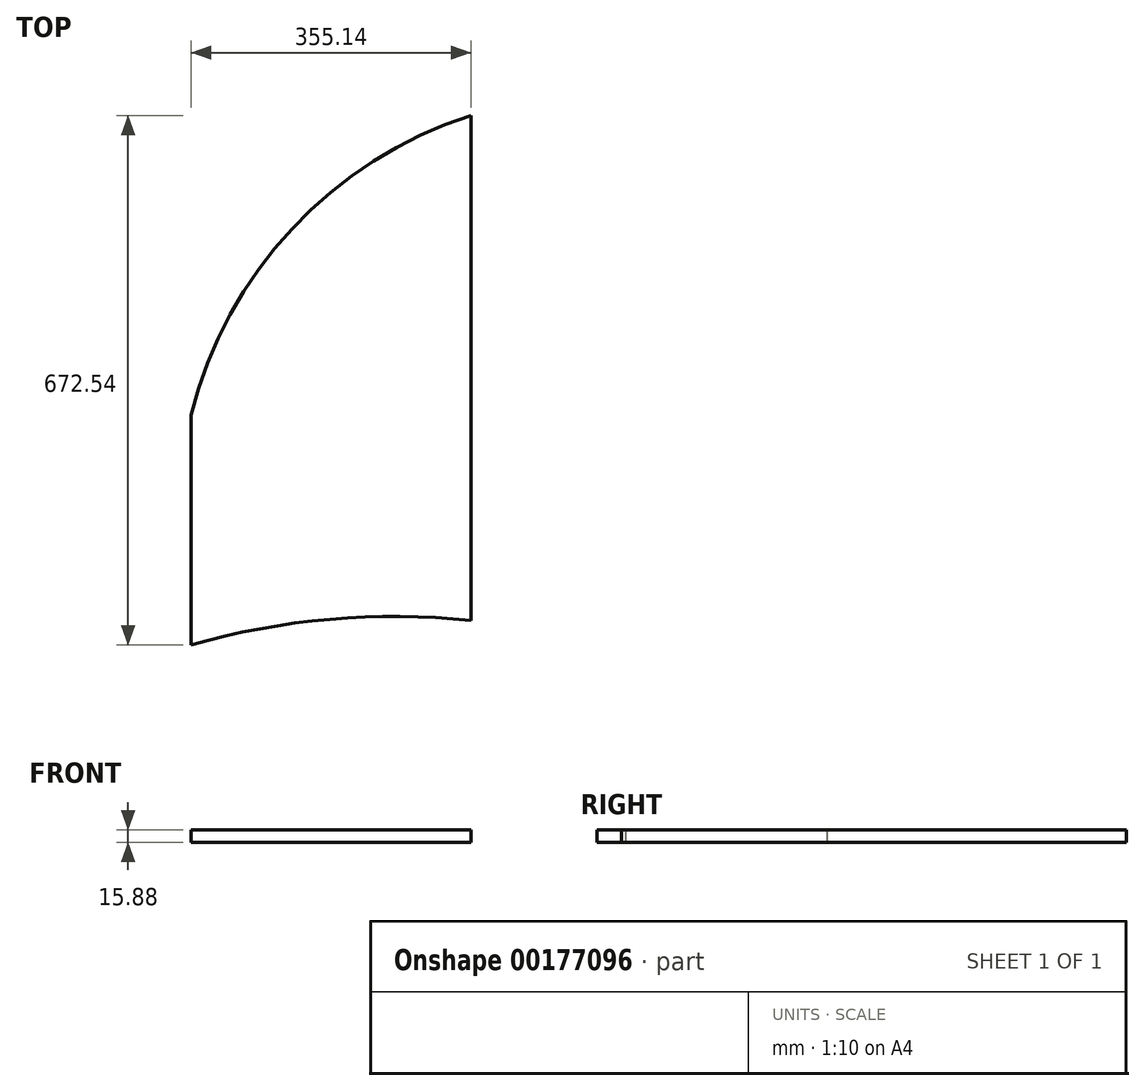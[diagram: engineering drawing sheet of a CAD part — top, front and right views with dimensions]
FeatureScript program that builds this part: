
annotation { "Feature Type Name" : "Feature", "Feature Type Description" : "" }
export const myFeature = defineFeature(function(context is Context, id is Id, definition is map)
    precondition{}
    {
        {
            var Q0;
            Q0=qCreatedBy(makeId("Top.planeOp"),FACE);
            var sketch = newSketch(context, id + "F0", { "sketchPlane" : qUnion([Q0])});
            skLineSegment(sketch, "E0", {"start": v(0, 641.35) * mm, "end": v(0, 0) * mm});
            skArc(sketch, "E1", {"start": v(0, 641.35) * mm, "mid": v(-227.12, 497.38) * mm, "end": v(-355.14, 260.91) * mm});
            skLineSegment(sketch, "E2", {"start": v(-355.14, -31.19) * mm, "end": v(-355.14, 260.91) * mm});
            skArc(sketch, "E3", {"start": v(0, 0) * mm, "mid": v(-179.06, 1.4) * mm, "end": v(-355.14, -31.19) * mm});
            skSolve(sketch);
        }
        {
            var Q0;
            Q0 = qSketchRegion(id + "F0", true);
            extrude(context, id + "F1", {"entities" : qUnion([Q0]), "depth" : 15.88 * mm});
        }
    });
